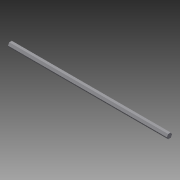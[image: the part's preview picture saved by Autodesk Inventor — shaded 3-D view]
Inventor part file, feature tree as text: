
AUTODESK INVENTOR PART (.ipt)
format: ipt  version: 2015 SP1 (Build 190203100, 203)  size: 77,312 bytes
history: native  units: in
note: dims shown in document units (in); Inventor stores cm internally (conversion verified against a paired STEP export)
features: extrude x1, sketch x1
ambient origin geometry x8: Origin, YZ Plane, XZ Plane, XY Plane, X Axis, Y Axis, Z Axis, Center Point
bodies: Solid1 (feature_tree)
feature tree (2):
  extrude  "Extrusion1"  Depth=0.5in
  sketch  "Sketch1"  dims[d0=0.5in d1=0.5in d2=0.5in d3=0.25in d4=120.0deg d5=120.0deg d6=0.25in d7=0.25in d8=17.75in d9=0.0in]
